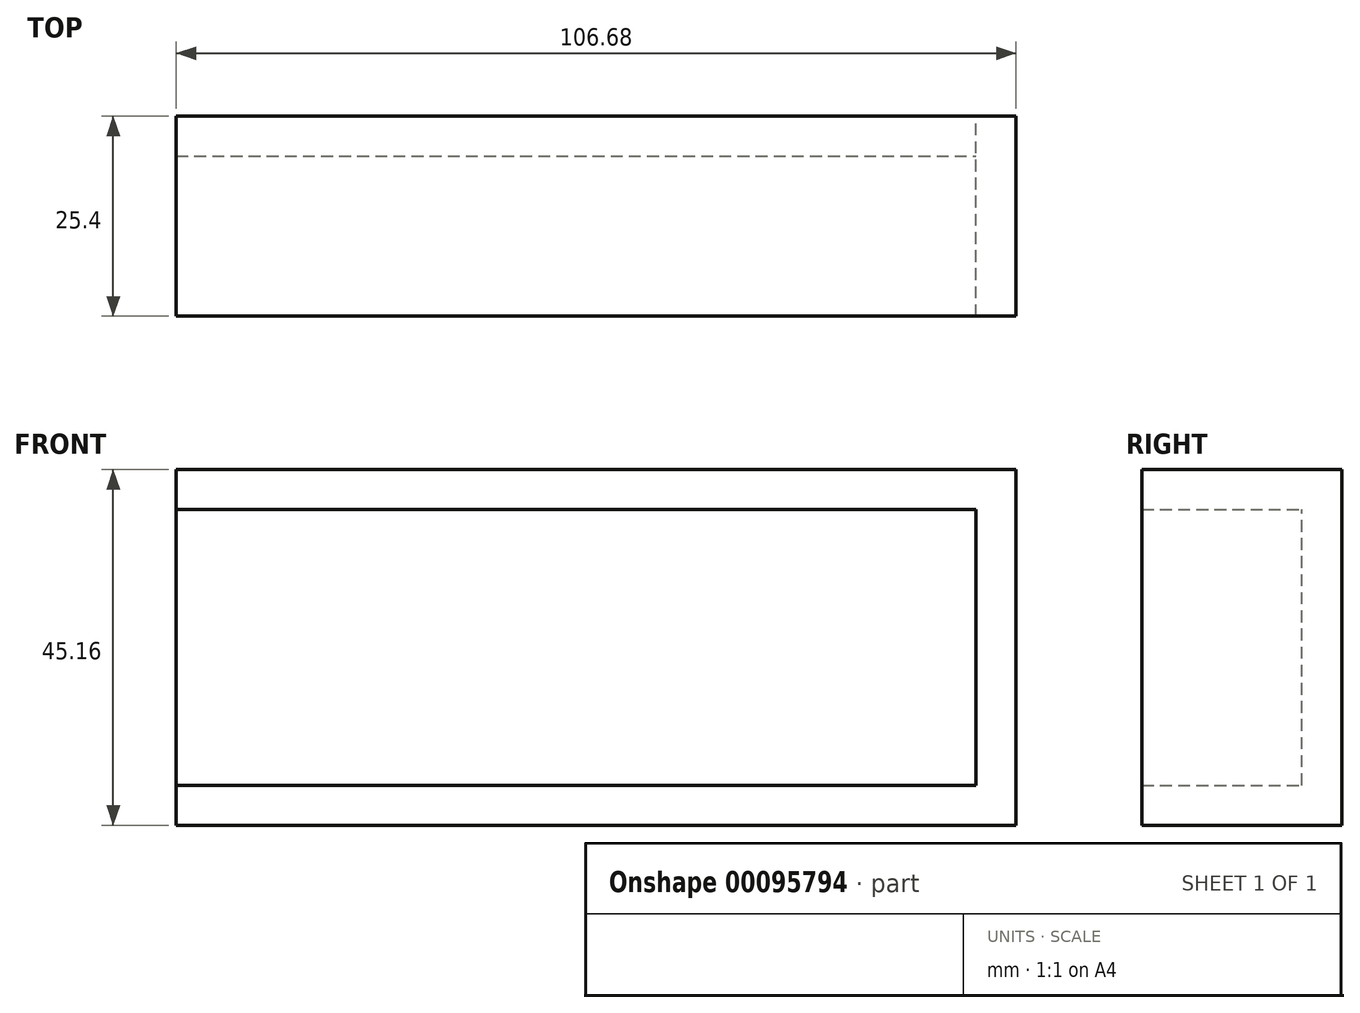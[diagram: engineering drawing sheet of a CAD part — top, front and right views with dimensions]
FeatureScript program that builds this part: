
annotation { "Feature Type Name" : "Feature", "Feature Type Description" : "" }
export const myFeature = defineFeature(function(context is Context, id is Id, definition is map)
    precondition{}
    {
        {
            var Q0;
            Q0=qCreatedBy(makeId("Front.planeOp"),FACE);
            var sketch = newSketch(context, id + "F0", { "sketchPlane" : qUnion([Q0])});
            skLineSegment(sketch, "E0.bottom", {"start": v(0, 0) * mm, "end": v(101.6, 0) * mm});
            skLineSegment(sketch, "E0.top", {"start": v(0, 35) * mm, "end": v(101.6, 35) * mm});
            skLineSegment(sketch, "E0.left", {"start": v(0, 0) * mm, "end": v(0, 35) * mm});
            skLineSegment(sketch, "E0.right", {"start": v(101.6, 0) * mm, "end": v(101.6, 35) * mm});
            skLineSegment(sketch, "E1.top", {"start": v(0, 40.08) * mm, "end": v(101.6, 40.08) * mm});
            skLineSegment(sketch, "E1.left", {"start": v(0, 35) * mm, "end": v(0, 40.08) * mm});
            skLineSegment(sketch, "E2.top", {"start": v(0, -5.08) * mm, "end": v(101.6, -5.08) * mm});
            skLineSegment(sketch, "E2.left", {"start": v(0, 0) * mm, "end": v(0, -5.08) * mm});
            skLineSegment(sketch, "E2.right", {"start": v(101.6, 0) * mm, "end": v(101.6, -5.08) * mm});
            skLineSegment(sketch, "E3.bottom", {"start": v(101.6, 40.08) * mm, "end": v(106.68, 40.08) * mm});
            skLineSegment(sketch, "E3.top", {"start": v(101.6, -5.08) * mm, "end": v(106.68, -5.08) * mm});
            skLineSegment(sketch, "E3.left", {"start": v(101.6, 40.08) * mm, "end": v(101.6, -5.08) * mm});
            skLineSegment(sketch, "E3.right", {"start": v(106.68, 40.08) * mm, "end": v(106.68, -5.08) * mm});
            skLineSegment(sketch, "E4.bottom", {"start": v(0, 40.08) * mm, "end": v(-5.08, 40.08) * mm});
            skLineSegment(sketch, "E4.top", {"start": v(0, -5.08) * mm, "end": v(-5.08, -5.08) * mm});
            skLineSegment(sketch, "E4.left", {"start": v(0, 35) * mm, "end": v(0, 0) * mm});
            skLineSegment(sketch, "E4.right", {"start": v(-5.08, 40.08) * mm, "end": v(-5.08, -5.08) * mm});
            skLineSegment(sketch, "E5.trimOffspring", {"start": v(0, -5.08) * mm, "end": v(0, -5.08) * mm});
            skSolve(sketch);
        }
        {
            var Q0;
            Q0 = qSketchRegion(id + "F0", true);
            extrude(context, id + "F1", {"entities" : qUnion([Q0]), "depth" : 25.4 * mm});
        }
        {
            var Q0;
            {var subQ0=sQuery(id+"F0.wireOp",EDGE,"E0.top");Q0=makeQuery(id+"F0.imprint","IMPRINT",FACE,{"disambiguationData":[TD([[makeQuery(id+"F0.imprint","IMPRINT",EDGE,{"derivedFrom":subQ0}),-1.0]])]});}
            extrude(context, id + "F2", {"entities" : qUnion([Q0]), "operationType" : NewBodyOperationType.ADD, "depth" : 5.08 * mm});
        }
        {
            var Q0;
            Q0=makeQuery(id+"F1.opExtrude","SWEPT_FACE",FACE,{"disambiguationData":[OSD([sQuery(id+"F0.wireOp",EDGE,"E4.right")])]});
            extrude(context, id + "F3", {"entities" : qUnion([Q0]), "operationType" : NewBodyOperationType.REMOVE, "oppositeDirection" : true, "depth" : 5.08 * mm});
        }
    });
